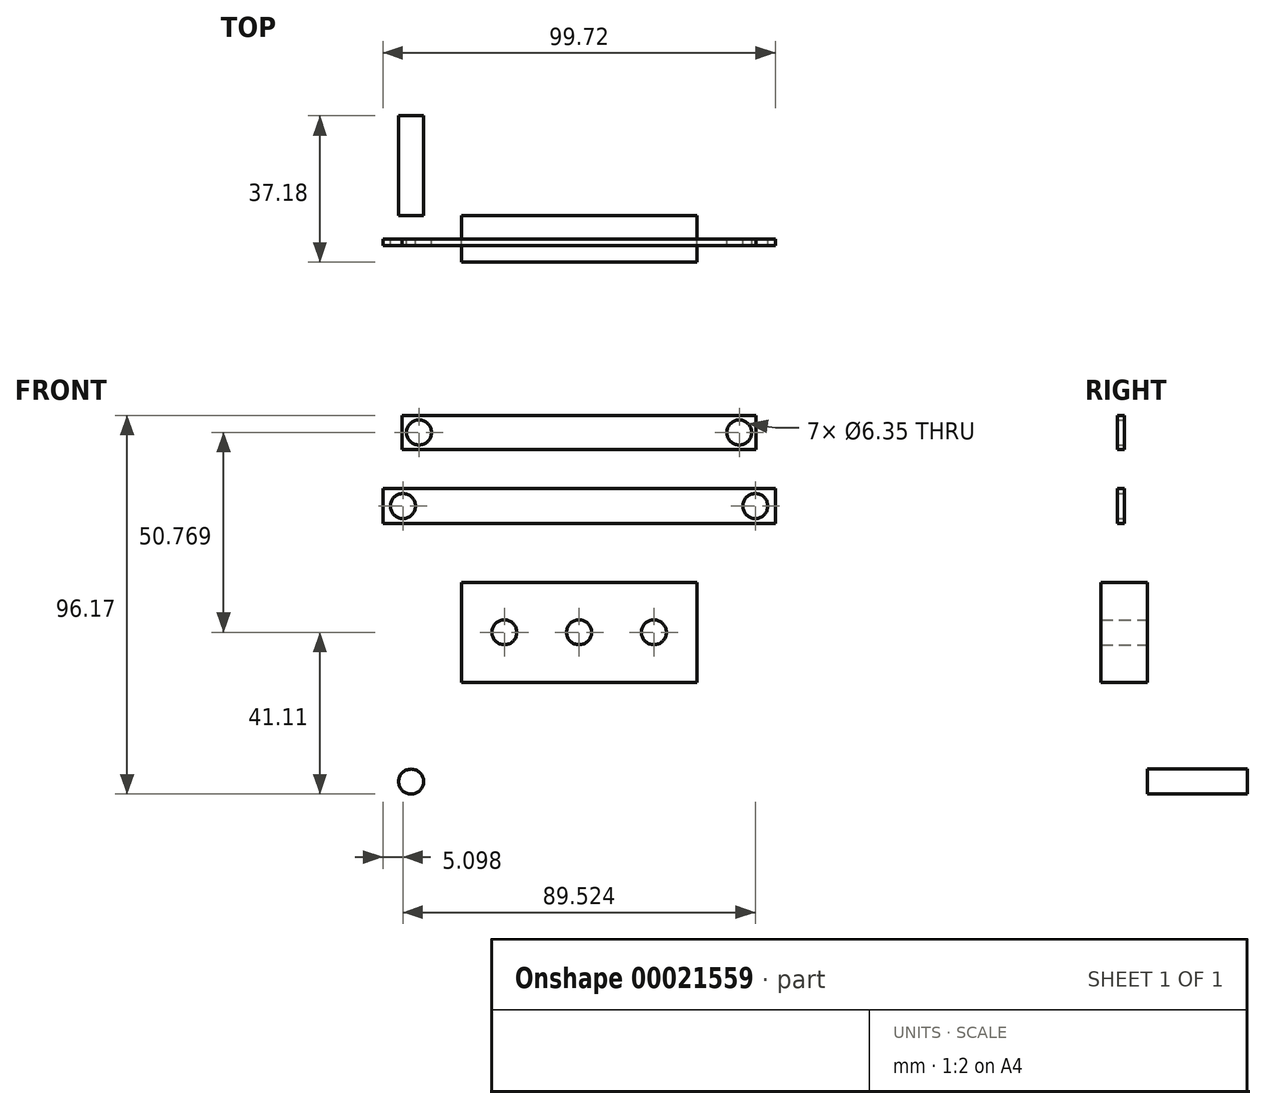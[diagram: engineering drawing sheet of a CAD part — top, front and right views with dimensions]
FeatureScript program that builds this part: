
annotation { "Feature Type Name" : "Feature", "Feature Type Description" : "" }
export const myFeature = defineFeature(function(context is Context, id is Id, definition is map)
    precondition{}
    {
        {
            var Q0;
            Q0=qCreatedBy(makeId("Top.planeOp"),FACE);
            var sketch = newSketch(context, id + "F0", { "sketchPlane" : qUnion([Q0])});
            skLineSegment(sketch, "E0.rect.bottom", {"start": v(29.92, -5.89) * mm, "end": v(-29.92, -5.89) * mm});
            skLineSegment(sketch, "E0.rect.top", {"start": v(29.92, 5.89) * mm, "end": v(-29.92, 5.89) * mm});
            skLineSegment(sketch, "E0.rect.left", {"start": v(29.92, -5.89) * mm, "end": v(29.92, 5.89) * mm});
            skLineSegment(sketch, "E0.rect.right", {"start": v(-29.92, -5.89) * mm, "end": v(-29.92, 5.89) * mm});
            skPoint(sketch, "E0.rect.middle", {"position": v(0, 0) * mm});
            skSolve(sketch);
        }
        {
            var Q0;
            Q0=makeQuery(id+"F0.imprint","IMPRINT",FACE,{"disambiguationData":[TD([[makeQuery(id+"F0.imprint","IMPRINT",EDGE,{"derivedFrom":sQuery(id+"F0.wireOp",EDGE,"E0.rect.bottom")}),-1.0]])]});
            extrude(context, id + "F1", {"entities" : qUnion([Q0]), "depth" : 25.4 * mm});
        }
        {
            var Q0;
            Q0=makeQuery(id+"F1.opExtrude","SWEPT_FACE",FACE,{"disambiguationData":[OSD([sQuery(id+"F0.wireOp",EDGE,"E0.rect.top")])]});
            var sketch = newSketch(context, id + "F2", { "sketchPlane" : qUnion([Q0])});
            skLineSegment(sketch, "E1", {"start": v(29.92, 12.7) * mm, "end": v(-29.92, 12.7) * mm});
            skCircle(sketch, "E2", {"center": v(0, 12.7) * mm, "radius": 10.93 * mm});
            skCircle(sketch, "E3", {"center": v(-29.92, 12.7) * mm, "radius": 10.93 * mm});
            skCircle(sketch, "E4", {"center": v(29.92, 12.7) * mm, "radius": 10.93 * mm});
            skPoint(sketch, "E5", {"position": v(19, 12.7) * mm});
            skPoint(sketch, "E6", {"position": v(-19, 12.7) * mm});
            skCircle(sketch, "E7", {"center": v(42.67, -25.24) * mm, "radius": 3.17 * mm});
            skSolve(sketch);
        }
        {
            var Q0;
            Q0=sQuery(id+"F2.wireOp",VERTEX,"E5");
            var Q1;
            Q1=sQuery(id+"F2.wireOp",VERTEX,"E6");
            var Q2;
            Q2=sQuery(id+"F2.wireOp",VERTEX,"E2.center");
            var Q3;
            Q3=makeQuery(id+"F1.opExtrude","SWEPT_BODY",BODY,{"disambiguationData":[OSD([sQuery(id+"F0.wireOp",EDGE,"E0.rect.bottom"),sQuery(id+"F0.wireOp",EDGE,"E0.rect.top"),sQuery(id+"F0.wireOp",EDGE,"E0.rect.left"),sQuery(id+"F0.wireOp",EDGE,"E0.rect.right")])]});
            hole(context, id + "F3", {"style" : HoleStyle.SIMPLE, "holeDiameter" : 6.35 * mm, "endStyle" : HoleEndStyle.THROUGH, "locations" : qUnion([Q0, Q1, Q2]), "scope" : qUnion([Q3])});
        }
        {
            var Q0;
            Q0=qCreatedBy(makeId("Front.planeOp"),FACE);
            var sketch = newSketch(context, id + "F4", { "sketchPlane" : qUnion([Q0])});
            skLineSegment(sketch, "E8.rect.bottom", {"start": v(49.86, 40.33) * mm, "end": v(-49.86, 40.33) * mm});
            skLineSegment(sketch, "E8.rect.top", {"start": v(49.86, 49.22) * mm, "end": v(-49.86, 49.22) * mm});
            skLineSegment(sketch, "E8.rect.left", {"start": v(49.86, 40.33) * mm, "end": v(49.86, 49.22) * mm});
            skLineSegment(sketch, "E8.rect.right", {"start": v(-49.86, 40.33) * mm, "end": v(-49.86, 49.22) * mm});
            skPoint(sketch, "E8.rect.middle", {"position": v(0, 44.78) * mm});
            skLineSegment(sketch, "E9.rect.bottom", {"start": v(44.95, 59.18) * mm, "end": v(-44.95, 59.18) * mm});
            skLineSegment(sketch, "E9.rect.top", {"start": v(44.95, 67.76) * mm, "end": v(-44.95, 67.76) * mm});
            skLineSegment(sketch, "E9.rect.left", {"start": v(44.95, 59.18) * mm, "end": v(44.95, 67.76) * mm});
            skLineSegment(sketch, "E9.rect.right", {"start": v(-44.95, 59.18) * mm, "end": v(-44.95, 67.76) * mm});
            skPoint(sketch, "E9.rect.middle", {"position": v(0, 63.47) * mm});
            skPoint(sketch, "E10", {"position": v(-40.68, 63.47) * mm});
            skPoint(sketch, "E11", {"position": v(-44.76, 44.78) * mm});
            skPoint(sketch, "E12.MirrorP", {"position": v(40.68, 63.47) * mm});
            skPoint(sketch, "E13.MirrorP", {"position": v(44.76, 44.78) * mm});
            skSolve(sketch);
        }
        {
            var Q0;
            Q0=makeQuery(id+"F4.imprint","IMPRINT",FACE,{"disambiguationData":[TD([[makeQuery(id+"F4.imprint","IMPRINT",EDGE,{"derivedFrom":sQuery(id+"F4.wireOp",EDGE,"E9.rect.bottom")}),-1.0]])]});
            var Q1;
            Q1=makeQuery(id+"F4.imprint","IMPRINT",FACE,{"disambiguationData":[TD([[makeQuery(id+"F4.imprint","IMPRINT",EDGE,{"derivedFrom":sQuery(id+"F4.wireOp",EDGE,"E8.rect.bottom")}),-1.0]])]});
            extrude(context, id + "F5", {"entities" : qUnion([Q0, Q1]), "depth" : 1.7 * mm});
        }
        {
            var Q0;
            Q0=sQuery(id+"F4.wireOp",VERTEX,"E10");
            var Q1;
            Q1=sQuery(id+"F4.wireOp",VERTEX,"E11");
            var Q2;
            Q2=sQuery(id+"F4.wireOp",VERTEX,"E12.MirrorP");
            var Q3;
            Q3=sQuery(id+"F4.wireOp",VERTEX,"E13.MirrorP");
            var Q4;
            Q4=makeQuery(id+"F5.opExtrude","SWEPT_BODY",BODY,{"disambiguationData":[OSD([sQuery(id+"F4.wireOp",EDGE,"E9.rect.bottom"),sQuery(id+"F4.wireOp",EDGE,"E9.rect.top"),sQuery(id+"F4.wireOp",EDGE,"E9.rect.left"),sQuery(id+"F4.wireOp",EDGE,"E9.rect.right")])]});
            var Q5;
            Q5=makeQuery(id+"F5.opExtrude","SWEPT_BODY",BODY,{"disambiguationData":[OSD([sQuery(id+"F4.wireOp",EDGE,"E8.rect.bottom"),sQuery(id+"F4.wireOp",EDGE,"E8.rect.top"),sQuery(id+"F4.wireOp",EDGE,"E8.rect.left"),sQuery(id+"F4.wireOp",EDGE,"E8.rect.right")])]});
            hole(context, id + "F6", {"style" : HoleStyle.SIMPLE, "holeDiameter" : 6.35 * mm, "endStyle" : HoleEndStyle.THROUGH, "oppositeDirection" : true, "locations" : qUnion([Q0, Q1, Q2, Q3]), "scope" : qUnion([Q4, Q5])});
        }
        {
            var Q0;
            Q0=makeQuery(id+"F2.imprint","IMPRINT",FACE,{"disambiguationData":[TD([[makeQuery(id+"F2.imprint","IMPRINT",EDGE,{"derivedFrom":sQuery(id+"F2.wireOp",EDGE,"E7")}),1.0]])]});
            extrude(context, id + "F7", {"entities" : qUnion([Q0]), "depth" : 25.4 * mm});
        }
    });
